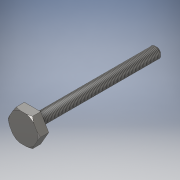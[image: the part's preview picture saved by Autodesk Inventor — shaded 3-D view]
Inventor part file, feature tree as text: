
AUTODESK INVENTOR PART (.ipt)
format: ipt  version: 2018 (Build 220112000, 112)  size: 142,848 bytes
history: native  units: in
note: dims shown in document units (in); Inventor stores cm internally (conversion verified against a paired STEP export)
features: sketch x4, extrude x3, revolve x1, chamfer x1, thread x1
ambient origin geometry x8: Origin, YZ Plane, XZ Plane, XY Plane, X Axis, Y Axis, Z Axis, Center Point
bodies: Solid1 (feature_tree)
feature tree (10):
  extrude  "Extrusion1"  Depth=10.05in TaperAngle=0.0deg
  extrude  "Extrusion2"  Depth=0.75in TaperAngle=0.0deg
  revolve  "Revolution1"  [1 undecoded]
  extrude  "Extrusion3"  TaperAngle=90.0deg  [1 undecoded]
  chamfer  "Chamfer1"  Distance=1.75in
  thread  "Thread1"  [1 undecoded]
  sketch  "Sketch1"  dims[d0=0.875in d1=10.05in d2=0.0in]
  sketch  "Sketch2"  dims[d3=1.3125in d4=0.75in d5=0.0in]
  sketch  "Sketch3"  dims[d6=0.875in d7=0.1in]
  sketch  "Sketch4"  dims[d8=0.15in d9=90.0deg d10=1.75in d11=0.05in d12=0.0in d13=0.125in d14=0.125in d15=45.0deg d16=1.0in d17=0.0in]
note: 3 required parameter values undecoded (feature->parameter linkage not recoverable at this tier; creation-order binding heuristic only, values carry confidence <= 0.55)